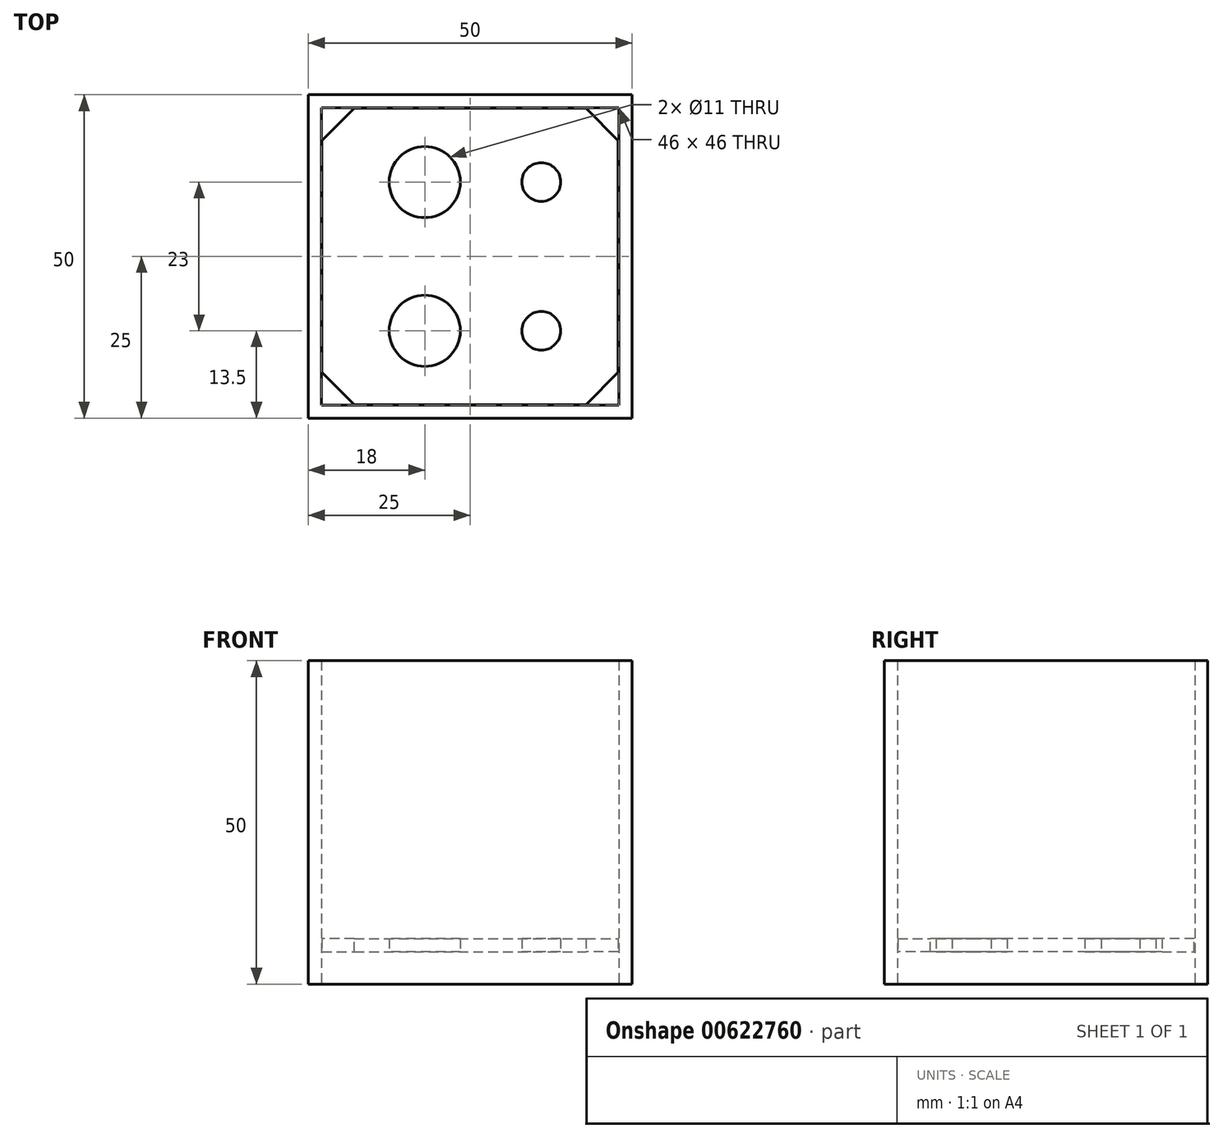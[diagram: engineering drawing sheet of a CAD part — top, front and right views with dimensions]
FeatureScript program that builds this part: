
annotation { "Feature Type Name" : "Feature", "Feature Type Description" : "" }
export const myFeature = defineFeature(function(context is Context, id is Id, definition is map)
    precondition{}
    {
        {
            var Q0;
            Q0=qCreatedBy(makeId("Top.planeOp"),FACE);
            var sketch = newSketch(context, id + "F0", { "sketchPlane" : qUnion([Q0])});
            skLineSegment(sketch, "E0.bottom", {"start": v(-25, 25) * mm, "end": v(25, 25) * mm});
            skLineSegment(sketch, "E0.top", {"start": v(-25, -25) * mm, "end": v(25, -25) * mm});
            skLineSegment(sketch, "E0.left", {"start": v(-25, 25) * mm, "end": v(-25, -25) * mm});
            skLineSegment(sketch, "E0.right", {"start": v(25, 25) * mm, "end": v(25, -25) * mm});
            skPoint(sketch, "E0.middle", {"position": v(0, 0) * mm});
            skLineSegment(sketch, "E1.bottom", {"start": v(-22.9, 22.9) * mm, "end": v(22.9, 22.9) * mm});
            skLineSegment(sketch, "E1.top", {"start": v(-22.9, -22.9) * mm, "end": v(22.9, -22.9) * mm});
            skLineSegment(sketch, "E1.left", {"start": v(-22.9, 22.9) * mm, "end": v(-22.9, -22.9) * mm});
            skLineSegment(sketch, "E1.right", {"start": v(22.9, 22.9) * mm, "end": v(22.9, -22.9) * mm});
            skLineSegment(sketch, "E2", {"start": v(-53.04, 0) * mm, "end": v(57.21, 0) * mm, "construction": true});
            skLineSegment(sketch, "E3", {"start": v(-7, 39.23) * mm, "end": v(-7, -33.23) * mm, "construction": true});
            skLineSegment(sketch, "E4", {"start": v(11, 38.45) * mm, "end": v(11, -32.71) * mm, "construction": true});
            skLineSegment(sketch, "E5", {"start": v(-34.28, 11.5) * mm, "end": v(43.4, 11.5) * mm, "construction": true});
            skCircle(sketch, "E6", {"center": v(-7, 11.5) * mm, "radius": 5.5 * mm});
            skCircle(sketch, "E7", {"center": v(11, 11.5) * mm, "radius": 3 * mm});
            skCircle(sketch, "E8.MirrorC", {"center": v(-7, -11.5) * mm, "radius": 5.5 * mm});
            skCircle(sketch, "E9.MirrorC", {"center": v(11, -11.5) * mm, "radius": 3 * mm});
            skLineSegment(sketch, "E10.bottom", {"start": v(-23, 23) * mm, "end": v(23, 23) * mm});
            skLineSegment(sketch, "E10.top", {"start": v(-23, -23) * mm, "end": v(23, -23) * mm});
            skLineSegment(sketch, "E10.left", {"start": v(-23, 23) * mm, "end": v(-23, -23) * mm});
            skLineSegment(sketch, "E10.right", {"start": v(23, 23) * mm, "end": v(23, -23) * mm});
            skPoint(sketch, "E11", {"position": v(25, 0) * mm});
            skPoint(sketch, "E12", {"position": v(23, 0) * mm});
            skLineSegment(sketch, "E13", {"start": v(25, 0) * mm, "end": v(23, 0) * mm});
            skSolve(sketch);
        }
        {
            var Q0;
            Q0=makeQuery(id+"F0.imprint","IMPRINT",FACE,{"disambiguationData":[TD([[makeQuery(id+"F0.imprint","IMPRINT",EDGE,{"derivedFrom":sQuery(id+"F0.wireOp",EDGE,"E1.bottom")}),-1.0]])]});
            extrude(context, id + "F1", {"entities" : qUnion([Q0]), "depth" : 2 * mm, "offsetDistance" : 25 * mm});
        }
        {
            var Q0;
            Q0=makeQuery(id+"F1.opExtrude","SWEPT_EDGE",EDGE,{"disambiguationData":[OSD([sQuery(id+"F0.wireOp",EDGE,"E1.bottom"),sQuery(id+"F0.wireOp",EDGE,"E1.right")])]});
            var Q1;
            Q1=makeQuery(id+"F1.opExtrude","SWEPT_EDGE",EDGE,{"disambiguationData":[OSD([sQuery(id+"F0.wireOp",EDGE,"E1.top"),sQuery(id+"F0.wireOp",EDGE,"E1.right")])]});
            var Q2;
            Q2=makeQuery(id+"F1.opExtrude","SWEPT_EDGE",EDGE,{"disambiguationData":[OSD([sQuery(id+"F0.wireOp",EDGE,"E1.top"),sQuery(id+"F0.wireOp",EDGE,"E1.left")])]});
            var Q3;
            Q3=makeQuery(id+"F1.opExtrude","SWEPT_EDGE",EDGE,{"disambiguationData":[OSD([sQuery(id+"F0.wireOp",EDGE,"E1.bottom"),sQuery(id+"F0.wireOp",EDGE,"E1.left")])]});
            chamfer(context, id + "F2", {"entities" : qUnion([Q0, Q1, Q2, Q3]), "width" : 5 * mm, "tangentPropagation" : true});
        }
        {
            var Q0;
            Q0=makeQuery(id+"F0.imprint","IMPRINT",FACE,{"disambiguationData":[TD([[makeQuery(id+"F0.imprint","IMPRINT",EDGE,{"derivedFrom":sQuery(id+"F0.wireOp",EDGE,"E0.bottom")}),-1.0]])]});
            extrude(context, id + "F3", {"entities" : qUnion([Q0]), "depth" : 50 * mm, "offsetDistance" : 25 * mm});
        }
        {
            var Q0;
            Q0=makeQuery(id+"F3.opExtrude","SWEPT_BODY",BODY,{"disambiguationData":[OSD([sQuery(id+"F0.wireOp",EDGE,"E0.bottom"),sQuery(id+"F0.wireOp",EDGE,"E0.top"),sQuery(id+"F0.wireOp",EDGE,"E0.left"),sQuery(id+"F0.wireOp",EDGE,"E0.right"),sQuery(id+"F0.wireOp",EDGE,"E10.bottom"),sQuery(id+"F0.wireOp",EDGE,"E10.top"),sQuery(id+"F0.wireOp",EDGE,"E10.left"),sQuery(id+"F0.wireOp",EDGE,"E10.right")])]});
            transform(context, id + "F4", {"entities" : qUnion([Q0]), "transformType" : TransformType.TRANSLATION_3D, "dx" : 0 * mm, "dy" : 0 * mm, "dz" : -5 * mm, "makeCopy" : false});
        }
    });
